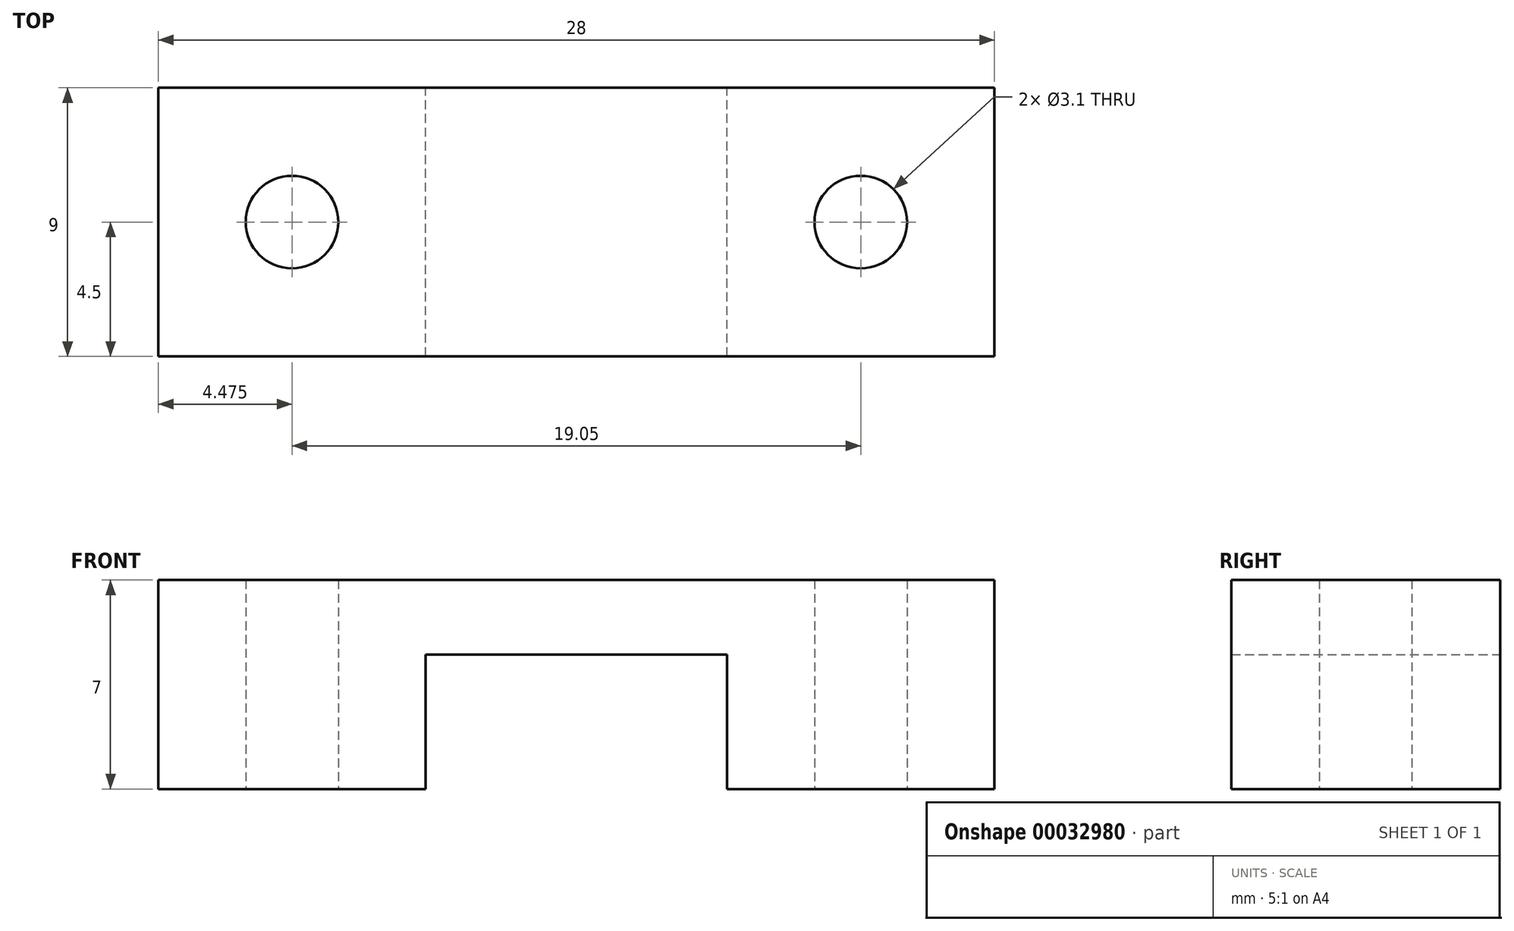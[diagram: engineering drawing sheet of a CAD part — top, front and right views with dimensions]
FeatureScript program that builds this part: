
annotation { "Feature Type Name" : "Feature", "Feature Type Description" : "" }
export const myFeature = defineFeature(function(context is Context, id is Id, definition is map)
    precondition{}
    {
        {
            var Q0;
            Q0=qCreatedBy(makeId("Front.planeOp"),FACE);
            var sketch = newSketch(context, id + "F0", { "sketchPlane" : qUnion([Q0])});
            skLineSegment(sketch, "E0.rect.bottom", {"start": v(14, -3.5) * mm, "end": v(-14, -3.5) * mm, "construction": true});
            skLineSegment(sketch, "E0.rect.top", {"start": v(14, 3.5) * mm, "end": v(-14, 3.5) * mm, "construction": true});
            skLineSegment(sketch, "E0.rect.left", {"start": v(14, -3.5) * mm, "end": v(14, 3.5) * mm, "construction": true});
            skLineSegment(sketch, "E0.rect.right", {"start": v(-14, -3.5) * mm, "end": v(-14, 3.5) * mm, "construction": true});
            skPoint(sketch, "E0.rect.middle", {"position": v(0, 0) * mm});
            skLineSegment(sketch, "E1", {"start": v(-14, 1) * mm, "end": v(14, 1) * mm, "construction": true});
            skLineSegment(sketch, "E2", {"start": v(5.05, 3.5) * mm, "end": v(5.05, -3.5) * mm, "construction": true});
            skLineSegment(sketch, "E3", {"start": v(0, 3.5) * mm, "end": v(14, 3.5) * mm});
            skLineSegment(sketch, "E4", {"start": v(14, -3.5) * mm, "end": v(14, 3.5) * mm});
            skLineSegment(sketch, "E5", {"start": v(14, -3.5) * mm, "end": v(5.05, -3.5) * mm});
            skLineSegment(sketch, "E6", {"start": v(5.05, 1) * mm, "end": v(0, 1) * mm});
            skLineSegment(sketch, "E7", {"start": v(5.05, 1) * mm, "end": v(5.05, -3.5) * mm});
            skLineSegment(sketch, "E8.MirrorCS", {"start": v(0, 3.5) * mm, "end": v(-14, 3.5) * mm});
            skLineSegment(sketch, "E9.MirrorCS", {"start": v(-14, -3.5) * mm, "end": v(-14, 3.5) * mm});
            skLineSegment(sketch, "E10.MirrorCS", {"start": v(-14, -3.5) * mm, "end": v(-5.05, -3.5) * mm});
            skLineSegment(sketch, "E11.MirrorCS", {"start": v(-5.05, 1) * mm, "end": v(-5.05, -3.5) * mm});
            skLineSegment(sketch, "E12.MirrorCS", {"start": v(-5.05, 1) * mm, "end": v(0, 1) * mm});
            skLineSegment(sketch, "E13", {"start": v(9.52, -3.5) * mm, "end": v(9.52, 3.5) * mm, "construction": true});
            skLineSegment(sketch, "E14", {"start": v(8.03, 3.5) * mm, "end": v(8.03, -3.5) * mm, "construction": true});
            skLineSegment(sketch, "E15.MirrorCS", {"start": v(11.02, 3.5) * mm, "end": v(11.02, -3.5) * mm, "construction": true});
            skSolve(sketch);
        }
        {
            var Q0;
            Q0=makeQuery(id+"F0.imprint","IMPRINT",FACE,{"disambiguationData":[TD([[makeQuery(id+"F0.imprint","IMPRINT",EDGE,{"derivedFrom":sQuery(id+"F0.wireOp",EDGE,"E3")}),-1.0]])]});
            extrude(context, id + "F1", {"entities" : qUnion([Q0]), "depth" : 9 * mm, "symmetric" : true});
        }
        {
            var Q0;
            Q0=makeQuery(id+"F1.opExtrude","SWEPT_FACE",FACE,{"disambiguationData":[OSD([sQuery(id+"F0.wireOp",EDGE,"E5")])]});
            var sketch = newSketch(context, id + "F2", { "sketchPlane" : qUnion([Q0])});
            skLineSegment(sketch, "E16", {"start": v(9.52, -4.5) * mm, "end": v(9.52, 4.5) * mm, "construction": true});
            skCircle(sketch, "E17", {"center": v(9.52, 0) * mm, "radius": 1.55 * mm});
            skCircle(sketch, "E18.MirrorC", {"center": v(-9.53, 0) * mm, "radius": 1.55 * mm});
            skSolve(sketch);
        }
        {
            var Q0;
            Q0=qSketchRegion(id+"F2",true);
            extrude(context, id + "F3", {"entities" : qUnion([Q0]), "operationType" : NewBodyOperationType.REMOVE, "endBound" : BoundingType.UP_TO_NEXT, "oppositeDirection" : true, "depth" : 25 * mm});
        }
    });
